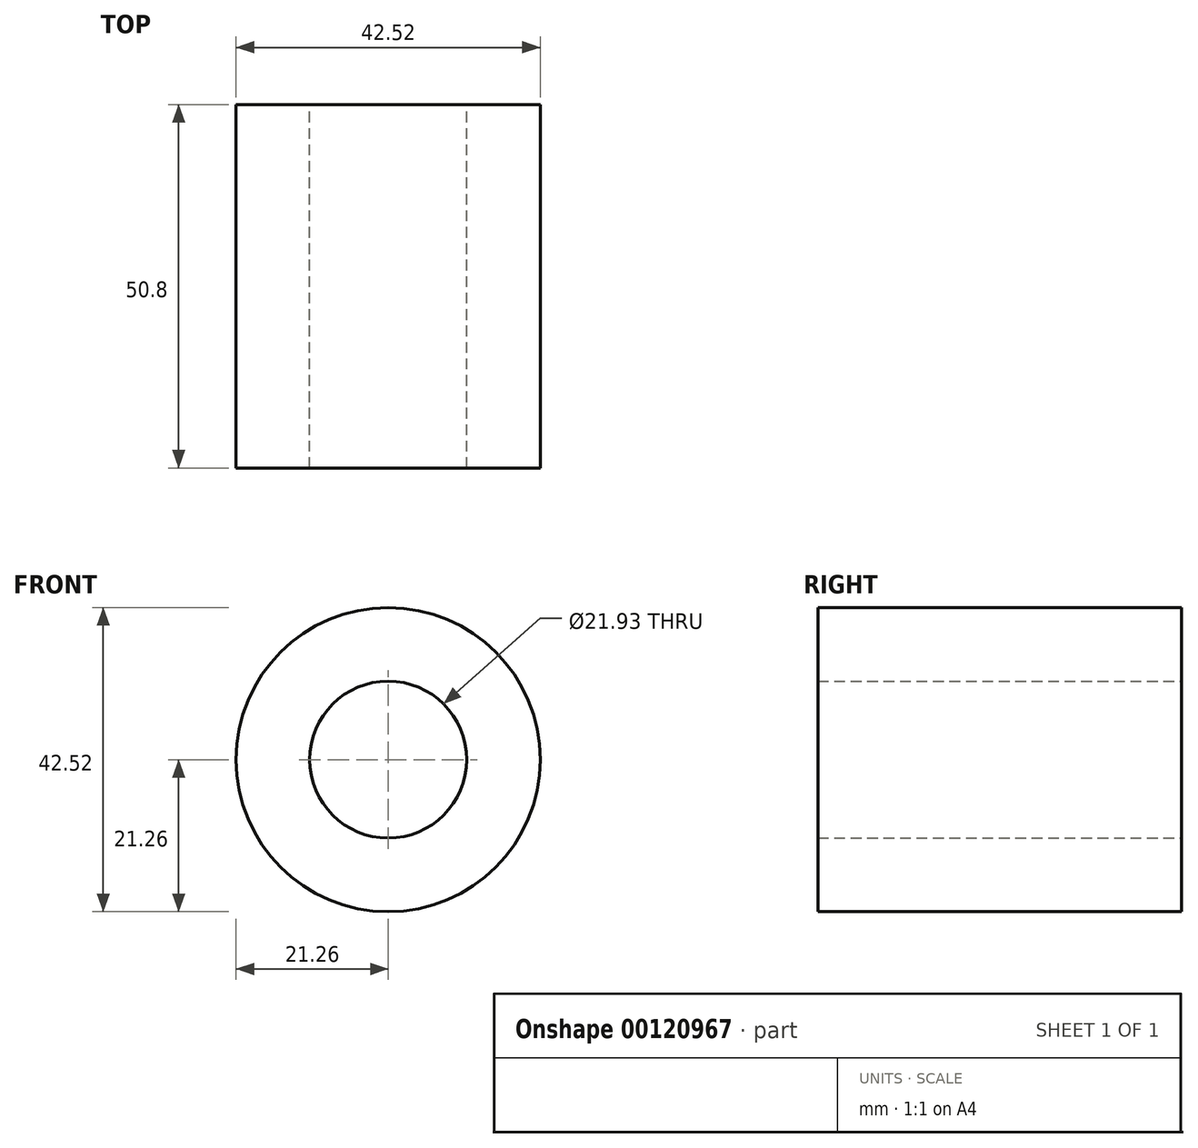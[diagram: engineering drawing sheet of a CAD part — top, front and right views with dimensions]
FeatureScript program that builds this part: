
annotation { "Feature Type Name" : "Feature", "Feature Type Description" : "" }
export const myFeature = defineFeature(function(context is Context, id is Id, definition is map)
    precondition{}
    {
        {
            var Q0;
            Q0=qCreatedBy(makeId("Front.planeOp"),FACE);
            var sketch = newSketch(context, id + "F0", { "sketchPlane" : qUnion([Q0])});
            skCircle(sketch, "E0", {"center": v(0, 0) * mm, "radius": 21.26 * mm});
            skCircle(sketch, "E1", {"center": v(0, 0) * mm, "radius": 10.84 * mm});
            skCircle(sketch, "E2", {"center": v(0, 0) * mm, "radius": 10.97 * mm});
            skCircle(sketch, "E3", {"center": v(0, 0) * mm, "radius": 10.42 * mm});
            skSolve(sketch);
        }
        {
            var Q0;
            Q0=makeQuery(id+"F0.imprint","IMPRINT",FACE,{"disambiguationData":[TD([[makeQuery(id+"F0.imprint","IMPRINT",EDGE,{"derivedFrom":sQuery(id+"F0.wireOp",EDGE,"E0")}),1.0]])]});
            extrude(context, id + "F1", {"entities" : qUnion([Q0]), "depth" : 50.8 * mm});
        }
    });
